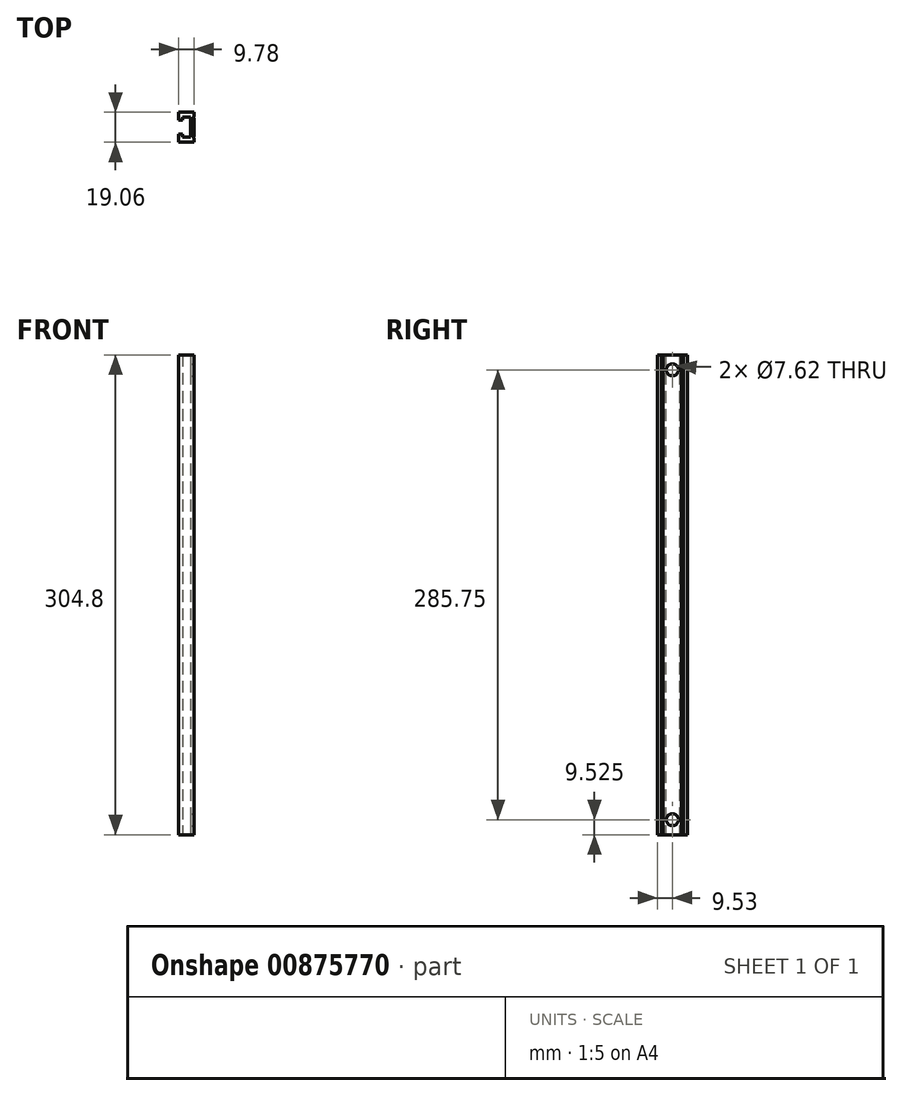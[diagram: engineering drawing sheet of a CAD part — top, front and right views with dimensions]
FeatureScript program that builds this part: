
annotation { "Feature Type Name" : "Feature", "Feature Type Description" : "" }
export const myFeature = defineFeature(function(context is Context, id is Id, definition is map)
    precondition{}
    {
        {
            var Q0;
            Q0=qCreatedBy(makeId("Top.planeOp"),FACE);
            var sketch = newSketch(context, id + "F0", { "sketchPlane" : qUnion([Q0])});
            skLineSegment(sketch, "E0.bottom", {"start": v(4.89, -9.52) * mm, "end": v(-4.89, -9.53) * mm});
            skLineSegment(sketch, "E0.top", {"start": v(4.89, 9.53) * mm, "end": v(-4.89, 9.53) * mm});
            skLineSegment(sketch, "E0.left", {"start": v(4.89, -9.52) * mm, "end": v(4.89, -6.86) * mm});
            skLineSegment(sketch, "E0.right", {"start": v(-4.89, -9.53) * mm, "end": v(-4.89, -4.45) * mm});
            skPoint(sketch, "E0.middle", {"position": v(0, 0) * mm});
            skLineSegment(sketch, "E1.bottom", {"start": v(-2.54, -4.45) * mm, "end": v(-4.89, -4.45) * mm});
            skLineSegment(sketch, "E1.top", {"start": v(-2.54, 4.45) * mm, "end": v(-4.89, 4.45) * mm});
            skPoint(sketch, "E1.middle", {"position": v(-4.89, 0) * mm});
            skLineSegment(sketch, "E2.bottom", {"start": v(2.54, -6.35) * mm, "end": v(-2.54, -6.35) * mm});
            skLineSegment(sketch, "E2.top", {"start": v(2.54, 6.35) * mm, "end": v(-2.54, 6.35) * mm});
            skLineSegment(sketch, "E2.left", {"start": v(2.54, -6.35) * mm, "end": v(2.54, 6.35) * mm});
            skLineSegment(sketch, "E2.right", {"start": v(-2.54, -6.35) * mm, "end": v(-2.54, -4.45) * mm});
            skLineSegment(sketch, "E3.trimOffspring", {"start": v(-4.89, 4.45) * mm, "end": v(-4.89, 9.53) * mm});
            skLineSegment(sketch, "E4.trimOffspring", {"start": v(-2.54, 4.45) * mm, "end": v(-2.54, 6.35) * mm});
            skPoint(sketch, "E5.orphan", {"position": v(-1.71, -4.45) * mm});
            skPoint(sketch, "E6.orphan", {"position": v(-1.71, 4.45) * mm});
            skPoint(sketch, "E7.orphan", {"position": v(-8.06, 4.45) * mm});
            skPoint(sketch, "E8.orphan", {"position": v(-8.06, -4.44) * mm});
            skArc(sketch, "E9", {"start": v(4.89, -5.87) * mm, "mid": v(4.6, -6.37) * mm, "end": v(4.89, -6.86) * mm});
            skArc(sketch, "E10.MirrorCS", {"start": v(4.89, 5.87) * mm, "mid": v(4.6, 6.37) * mm, "end": v(4.89, 6.86) * mm});
            skLineSegment(sketch, "E11.trimOffspring", {"start": v(4.89, 6.86) * mm, "end": v(4.89, 9.53) * mm});
            skLineSegment(sketch, "E12.trimOffspring", {"start": v(4.89, -5.87) * mm, "end": v(4.89, 5.87) * mm});
            skSolve(sketch);
        }
        {
            var Q0;
            Q0=qSketchRegion(id+"F0",true);
            extrude(context, id + "F1", {"entities" : qUnion([Q0]), "depth" : 304.8 * mm, "offsetDistance" : 25.4 * mm});
        }
        {
            var Q0;
            Q0=makeQuery(id+"F1.opExtrude","SWEPT_FACE",FACE,{"disambiguationData":[OSD([sQuery(id+"F0.wireOp",EDGE,"E12.trimOffspring")])]});
            var sketch = newSketch(context, id + "F2", { "sketchPlane" : qUnion([Q0])});
            skPoint(sketch, "E13", {"position": v(0, 295.28) * mm});
            skPoint(sketch, "E13.positionSnap0", {"position": v(0, 304.8) * mm});
            skPoint(sketch, "E14", {"position": v(0, 142.88) * mm});
            skPoint(sketch, "E15", {"position": v(0, 73.03) * mm});
            skPoint(sketch, "E16", {"position": v(0, 9.53) * mm});
            skSolve(sketch);
        }
        {
            var Q0;
            Q0=sQuery(id+"F2.wireOp",VERTEX,"E13");
            var Q1;
            Q1=sQuery(id+"F2.wireOp",VERTEX,"E16");
            var Q2;
            Q2=makeQuery(id+"F1.opExtrude","SWEPT_BODY",BODY,{"disambiguationData":[OSD([sQuery(id+"F0.wireOp",EDGE,"E0.bottom"),sQuery(id+"F0.wireOp",EDGE,"E0.top"),sQuery(id+"F0.wireOp",EDGE,"E0.left"),sQuery(id+"F0.wireOp",EDGE,"E0.right"),sQuery(id+"F0.wireOp",EDGE,"E1.bottom"),sQuery(id+"F0.wireOp",EDGE,"E1.top"),sQuery(id+"F0.wireOp",EDGE,"E2.bottom"),sQuery(id+"F0.wireOp",EDGE,"E2.top"),sQuery(id+"F0.wireOp",EDGE,"E2.left"),sQuery(id+"F0.wireOp",EDGE,"E2.right"),sQuery(id+"F0.wireOp",EDGE,"E3.trimOffspring"),sQuery(id+"F0.wireOp",EDGE,"E4.trimOffspring"),sQuery(id+"F0.wireOp",EDGE,"E9"),sQuery(id+"F0.wireOp",EDGE,"E10.MirrorCS"),sQuery(id+"F0.wireOp",EDGE,"E11.trimOffspring"),sQuery(id+"F0.wireOp",EDGE,"E12.trimOffspring")])]});
            hole(context, id + "F3", {"style" : HoleStyle.SIMPLE, "endStyle" : HoleEndStyle.BLIND, "holeDiameter" : 7.62 * mm, "majorDiameter" : 6.35 * mm, "holeDepth" : 25.4 * mm, "tappedDepth" : 76.2 * mm, "tapClearance" : 3, "startFromSketch" : true, "locations" : qUnion([Q0, Q1]), "scope" : qUnion([Q2])});
        }
    });
